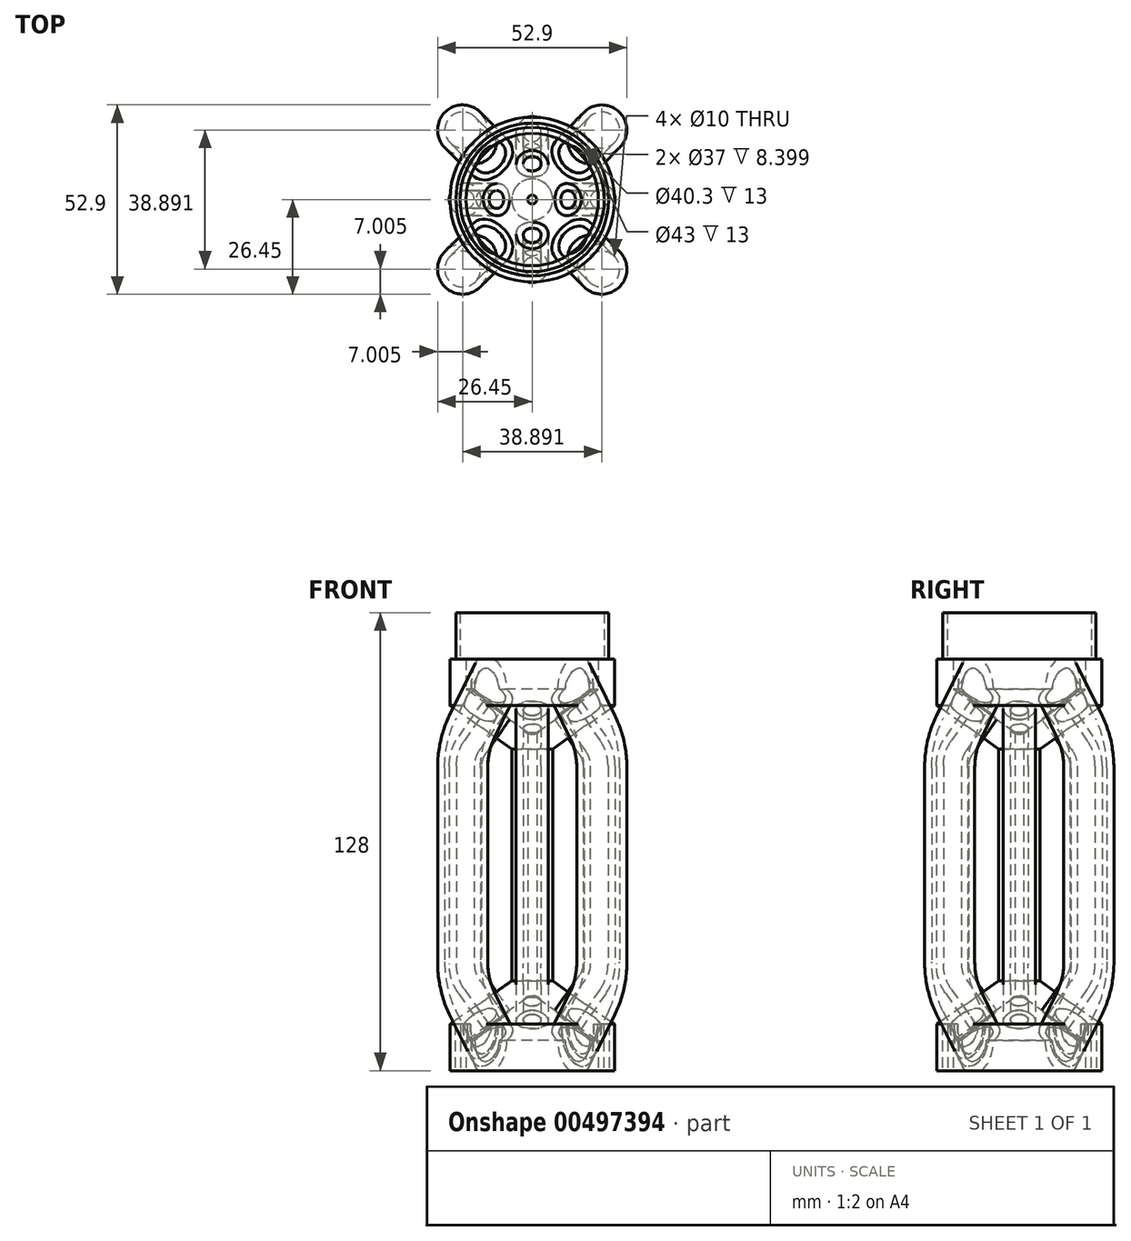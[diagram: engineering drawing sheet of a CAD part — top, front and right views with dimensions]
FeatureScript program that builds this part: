
annotation { "Feature Type Name" : "Feature", "Feature Type Description" : "" }
export const myFeature = defineFeature(function(context is Context, id is Id, definition is map)
    precondition{}
    {
        {
            var Q0;
            Q0=qCreatedBy(makeId("Front.planeOp"),FACE);
            var sketch = newSketch(context, id + "F0", { "sketchPlane" : qUnion([Q0])});
            skLineSegment(sketch, "E0", {"start": v(0, 0) * mm, "end": v(23, 0) * mm});
            skLineSegment(sketch, "E1.bottom", {"start": v(23, 0) * mm, "end": v(21.5, 0) * mm});
            skLineSegment(sketch, "E1.top", {"start": v(23, -13) * mm, "end": v(21.5, -13) * mm});
            skLineSegment(sketch, "E1.left", {"start": v(23, 0) * mm, "end": v(23, -13) * mm});
            skLineSegment(sketch, "E1.right", {"start": v(21.5, 0) * mm, "end": v(21.5, -13) * mm});
            skLineSegment(sketch, "E2.bottom", {"start": v(21.5, 0) * mm, "end": v(20, 0) * mm});
            skLineSegment(sketch, "E2.top", {"start": v(21.5, -13) * mm, "end": v(20, -13) * mm});
            skLineSegment(sketch, "E2.right", {"start": v(20, 0) * mm, "end": v(20, -13) * mm});
            skLineSegment(sketch, "E3.bottom", {"start": v(20, -13) * mm, "end": v(18.5, -13) * mm});
            skLineSegment(sketch, "E3.top", {"start": v(20, 0) * mm, "end": v(18.5, 0) * mm});
            skLineSegment(sketch, "E3.left", {"start": v(20, -13) * mm, "end": v(20, 0) * mm});
            skLineSegment(sketch, "E3.right", {"start": v(18.5, -13) * mm, "end": v(18.5, 0) * mm});
            skLineSegment(sketch, "E4.bottom", {"start": v(23, 0) * mm, "end": v(0, 0) * mm});
            skLineSegment(sketch, "E4.top", {"start": v(23, 102) * mm, "end": v(0, 102) * mm});
            skLineSegment(sketch, "E4.left", {"start": v(23, 0) * mm, "end": v(23, 102) * mm});
            skLineSegment(sketch, "E4.right", {"start": v(0, 0) * mm, "end": v(0, 102) * mm});
            skLineSegment(sketch, "E5.bottom", {"start": v(21.35, 102) * mm, "end": v(20.15, 102) * mm});
            skLineSegment(sketch, "E5.top", {"start": v(21.35, 115) * mm, "end": v(20.15, 115) * mm});
            skLineSegment(sketch, "E5.left", {"start": v(21.35, 102) * mm, "end": v(21.35, 115) * mm});
            skLineSegment(sketch, "E5.right", {"start": v(20.15, 102) * mm, "end": v(20.15, 115) * mm});
            skLineSegment(sketch, "E6", {"start": v(0, 44.5) * mm, "end": v(23, 44.5) * mm});
            skLineSegment(sketch, "E7.0", {"start": v(18.5, 0) * mm, "end": v(18.5, 102) * mm});
            skPoint(sketch, "E8.endSnap0", {"position": v(11.5, 44.5) * mm});
            skLineSegment(sketch, "E9", {"start": v(11.5, 44.5) * mm, "end": v(0, 44.5) * mm});
            skPoint(sketch, "E10", {"position": v(5.75, 44.5) * mm});
            skLineSegment(sketch, "E11", {"start": v(23, 0) * mm, "end": v(5.75, 7.47) * mm});
            skLineSegment(sketch, "E12", {"start": v(5.75, 7.47) * mm, "end": v(5.75, 44.5) * mm});
            skLineSegment(sketch, "E13.0", {"start": v(1.25, 4.51) * mm, "end": v(1.25, 44.5) * mm});
            skLineSegment(sketch, "E13.1", {"start": v(20.46, -3.8) * mm, "end": v(1.25, 4.51) * mm});
            skLineSegment(sketch, "E14.MirrorCS", {"start": v(5.75, 81.53) * mm, "end": v(5.75, 44.5) * mm});
            skLineSegment(sketch, "E15.MirrorCS", {"start": v(1.25, 84.49) * mm, "end": v(1.25, 44.5) * mm});
            skLineSegment(sketch, "E16.MirrorCS", {"start": v(20.46, 92.8) * mm, "end": v(1.25, 84.49) * mm});
            skLineSegment(sketch, "E17.MirrorCS", {"start": v(23, 89) * mm, "end": v(5.75, 81.53) * mm});
            skLineSegment(sketch, "E18", {"start": v(23, 0) * mm, "end": v(5.75, 12.08) * mm});
            skLineSegment(sketch, "E19.0", {"start": v(19.36, -5.2) * mm, "end": v(-0.63, 8.8) * mm});
            skLineSegment(sketch, "E20", {"start": v(1.25, 7.48) * mm, "end": v(-0.55, 8.74) * mm});
            skLineSegment(sketch, "E21.MirrorCS", {"start": v(19.36, 94.2) * mm, "end": v(-0.63, 80.2) * mm});
            skLineSegment(sketch, "E22.MirrorCS", {"start": v(23, 89) * mm, "end": v(5.75, 76.92) * mm});
            skLineSegment(sketch, "E23.MirrorCS", {"start": v(1.25, 81.52) * mm, "end": v(-0.55, 80.26) * mm});
            skSolve(sketch);
        }
        {
            var Q0;
            Q0=makeQuery(id+"F0.imprint","IMPRINT",FACE,{"disambiguationData":[TD([[makeQuery(id+"F0.imprint","IMPRINT",EDGE,{"derivedFrom":sQuery(id+"F0.wireOp",EDGE,"E1.top")}),-1.0]])]});
            var Q1;
            {var subQ1=sQuery(id+"F0.wireOp",EDGE,"E3.bottom");Q1=makeQuery(id+"F0.imprint","IMPRINT",FACE,{"disambiguationData":[TD([[makeQuery(id+"F0.imprint","IMPRINT",EDGE,{"derivedFrom":subQ1}),-1.0]])]});}
            var Q2;
            {var subQ3=sQuery(id+"F0.wireOp",EDGE,"E0");var subQ6=makeQuery(id+"F0.imprint","INTERSECT",VERTEX,{"derivedFrom":[subQ3,sQuery(id+"F0.wireOp",EDGE,"E1.right")]});Q2=makeQuery(id+"F0.imprint","IMPRINT",FACE,{"disambiguationData":[TD([[makeQuery(id+"F0.imprint","IMPRINT",EDGE,{"disambiguationData":[TD([[subQ6,1.0]])],"derivedFrom":subQ3}),1.0]])]});}
            var Q3;
            {var subQ0=sQuery(id+"F0.wireOp",EDGE,"E4.top");var subQ7=sQuery(id+"F0.wireOp",EDGE,"E4.left");var subQ8=makeQuery(id+"F0.imprint","INTERSECT",VERTEX,{"derivedFrom":[subQ0,subQ7]});Q3=makeQuery(id+"F0.imprint","IMPRINT",FACE,{"disambiguationData":[TD([[makeQuery(id+"F0.imprint","IMPRINT",EDGE,{"disambiguationData":[TD([[subQ8,-1.0]])],"derivedFrom":subQ0}),1.0]])]});}
            var Q4;
            Q4=makeQuery(id+"F0.imprint","IMPRINT",FACE,{"disambiguationData":[TD([[makeQuery(id+"F0.imprint","IMPRINT",EDGE,{"derivedFrom":sQuery(id+"F0.wireOp",EDGE,"E5.top")}),1.0]])]});
            var Q5;
            {var subQ0=sQuery(id+"F0.wireOp",EDGE,"E2.right");var subQ5=sQuery(id+"F0.wireOp",EDGE,"E13.1");var subQ7=makeQuery(id+"F0.imprint","INTERSECT",VERTEX,{"derivedFrom":[subQ0,subQ5]});Q5=makeQuery(id+"F0.imprint","IMPRINT",FACE,{"disambiguationData":[TD([[makeQuery(id+"F0.imprint","IMPRINT",EDGE,{"disambiguationData":[TD([[subQ7,1.0]])],"derivedFrom":subQ0}),-1.0]])]});}
            var Q6;
            {var subQ3=sQuery(id+"F0.wireOp",EDGE,"E3.right");var subQ5=sQuery(id+"F0.wireOp",EDGE,"E13.1");var subQ7=makeQuery(id+"F0.imprint","INTERSECT",VERTEX,{"derivedFrom":[subQ3,subQ5]});Q6=makeQuery(id+"F0.imprint","IMPRINT",FACE,{"disambiguationData":[TD([[makeQuery(id+"F0.imprint","IMPRINT",EDGE,{"disambiguationData":[TD([[subQ7,-1.0]])],"derivedFrom":subQ5}),-1.0]])]});}
            var Q7;
            {var subQ0=sQuery(id+"F0.wireOp",EDGE,"E11");var subQ1=sQuery(id+"F0.wireOp",EDGE,"E7.0");var subQ2=makeQuery(id+"F0.imprint","INTERSECT",VERTEX,{"derivedFrom":[subQ1,subQ0]});Q7=makeQuery(id+"F0.imprint","IMPRINT",FACE,{"disambiguationData":[TD([[makeQuery(id+"F0.imprint","IMPRINT",EDGE,{"disambiguationData":[TD([[subQ2,-1.0]])],"derivedFrom":subQ0}),1.0]])]});}
            var Q8;
            {var subQ2=sQuery(id+"F0.wireOp",EDGE,"E17.MirrorCS");var subQ8=sQuery(id+"F0.wireOp",EDGE,"E7.0");var subQ9=makeQuery(id+"F0.imprint","INTERSECT",VERTEX,{"derivedFrom":[subQ8,subQ2]});Q8=makeQuery(id+"F0.imprint","IMPRINT",FACE,{"disambiguationData":[TD([[makeQuery(id+"F0.imprint","IMPRINT",EDGE,{"disambiguationData":[TD([[subQ9,-1.0]])],"derivedFrom":subQ8}),1.0]])]});}
            var Q9;
            {var subQ0=sQuery(id+"F0.wireOp",EDGE,"E18");var subQ1=sQuery(id+"F0.wireOp",EDGE,"E7.0");var subQ2=makeQuery(id+"F0.imprint","INTERSECT",VERTEX,{"derivedFrom":[subQ1,subQ0]});Q9=makeQuery(id+"F0.imprint","IMPRINT",FACE,{"disambiguationData":[TD([[makeQuery(id+"F0.imprint","IMPRINT",EDGE,{"disambiguationData":[TD([[subQ2,1.0]])],"derivedFrom":subQ1}),1.0]])]});}
            var Q10;
            {var subQ0=sQuery(id+"F0.wireOp",EDGE,"E18");var subQ1=sQuery(id+"F0.wireOp",EDGE,"E7.0");var subQ2=makeQuery(id+"F0.imprint","INTERSECT",VERTEX,{"derivedFrom":[subQ1,subQ0]});Q10=makeQuery(id+"F0.imprint","IMPRINT",FACE,{"disambiguationData":[TD([[makeQuery(id+"F0.imprint","IMPRINT",EDGE,{"disambiguationData":[TD([[subQ2,1.0]])],"derivedFrom":subQ1}),-1.0]])]});}
            var Q11;
            {var subQ0=sQuery(id+"F0.wireOp",EDGE,"E11");var subQ1=sQuery(id+"F0.wireOp",EDGE,"E7.0");var subQ2=makeQuery(id+"F0.imprint","INTERSECT",VERTEX,{"derivedFrom":[subQ1,subQ0]});Q11=makeQuery(id+"F0.imprint","IMPRINT",FACE,{"disambiguationData":[TD([[makeQuery(id+"F0.imprint","IMPRINT",EDGE,{"disambiguationData":[TD([[subQ2,-1.0]])],"derivedFrom":subQ0}),1.0]])]});}
            var Q12;
            {var subQ0=sQuery(id+"F0.wireOp",EDGE,"E13.1");var subQ1=sQuery(id+"F0.wireOp",EDGE,"E3.right");var subQ2=makeQuery(id+"F0.imprint","INTERSECT",VERTEX,{"derivedFrom":[subQ1,subQ0]});Q12=makeQuery(id+"F0.imprint","IMPRINT",FACE,{"disambiguationData":[TD([[makeQuery(id+"F0.imprint","IMPRINT",EDGE,{"disambiguationData":[TD([[subQ2,1.0]])],"derivedFrom":subQ1}),1.0]])]});}
            var Q13;
            {var subQ0=sQuery(id+"F0.wireOp",EDGE,"E17.MirrorCS");var subQ1=sQuery(id+"F0.wireOp",EDGE,"E7.0");var subQ2=makeQuery(id+"F0.imprint","INTERSECT",VERTEX,{"derivedFrom":[subQ1,subQ0]});Q13=makeQuery(id+"F0.imprint","IMPRINT",FACE,{"disambiguationData":[TD([[makeQuery(id+"F0.imprint","IMPRINT",EDGE,{"disambiguationData":[TD([[subQ2,1.0]])],"derivedFrom":subQ1}),1.0]])]});}
            var Q14;
            {var subQ2=sQuery(id+"F0.wireOp",EDGE,"E17.MirrorCS");var subQ8=sQuery(id+"F0.wireOp",EDGE,"E7.0");var subQ9=makeQuery(id+"F0.imprint","INTERSECT",VERTEX,{"derivedFrom":[subQ8,subQ2]});Q14=makeQuery(id+"F0.imprint","IMPRINT",FACE,{"disambiguationData":[TD([[makeQuery(id+"F0.imprint","IMPRINT",EDGE,{"disambiguationData":[TD([[subQ9,-1.0]])],"derivedFrom":subQ8}),1.0]])]});}
            var Q15;
            {var subQ0=sQuery(id+"F0.wireOp",EDGE,"E17.MirrorCS");var subQ1=sQuery(id+"F0.wireOp",EDGE,"E7.0");var subQ2=makeQuery(id+"F0.imprint","INTERSECT",VERTEX,{"derivedFrom":[subQ1,subQ0]});Q15=makeQuery(id+"F0.imprint","IMPRINT",FACE,{"disambiguationData":[TD([[makeQuery(id+"F0.imprint","IMPRINT",EDGE,{"disambiguationData":[TD([[subQ2,1.0]])],"derivedFrom":subQ1}),-1.0]])]});}
            var Q16;
            {var subQ0=sQuery(id+"F0.wireOp",EDGE,"E16.MirrorCS");var subQ1=sQuery(id+"F0.wireOp",EDGE,"E7.0");var subQ2=makeQuery(id+"F0.imprint","INTERSECT",VERTEX,{"derivedFrom":[subQ1,subQ0]});Q16=makeQuery(id+"F0.imprint","IMPRINT",FACE,{"disambiguationData":[TD([[makeQuery(id+"F0.imprint","IMPRINT",EDGE,{"disambiguationData":[TD([[subQ2,-1.0]])],"derivedFrom":subQ1}),1.0]])]});}
            var Q17;
            Q17=sQuery(id+"F0.wireOp",EDGE,"E4.right");
            revolve(context, id + "F1", {"entities" : qUnion([Q0, Q1, Q2, Q3, Q4, Q5, Q6, Q7, Q8, Q9, Q10, Q11, Q12, Q13, Q14, Q15, Q16]), "axis" : qUnion([Q17]), "revolveType" : RevolveType.FULL, "surfaceOperationType" : NewSurfaceOperationType.NEW});
        }
        {
            var Q0;
            Q0=makeQuery(id+"F1.opRevolve","SWEPT_FACE",FACE,{"disambiguationData":[OSD([sQuery(id+"F0.wireOp",EDGE,"E3.bottom")])]});
            var sketch = newSketch(context, id + "F2", { "sketchPlane" : qUnion([Q0])});
            skCircle(sketch, "E24.0", {"center": v(0, 0) * mm, "radius": 18.5 * mm});
            skLineSegment(sketch, "E25", {"start": v(18.5, 0) * mm, "end": v(-18.5, 0) * mm});
            skLineSegment(sketch, "E26", {"start": v(0, 18.5) * mm, "end": v(0, -18.5) * mm});
            skLineSegment(sketch, "E27", {"start": v(0, 0) * mm, "end": v(18.5, 0) * mm});
            skLineSegment(sketch, "E28", {"start": v(0, -18.5) * mm, "end": v(0, 0) * mm});
            skLineSegment(sketch, "E29", {"start": v(-18.5, 0) * mm, "end": v(0, 0) * mm});
            skLineSegment(sketch, "E30", {"start": v(0, 0) * mm, "end": v(0, 18.5) * mm});
            skPoint(sketch, "E31", {"position": v(9.25, 0) * mm});
            skPoint(sketch, "E32", {"position": v(0, -9.25) * mm});
            skPoint(sketch, "E33", {"position": v(-9.25, 0) * mm});
            skPoint(sketch, "E34", {"position": v(0, 9.25) * mm});
            skLineSegment(sketch, "E35", {"start": v(-9.25, 0) * mm, "end": v(-18.5, 0) * mm});
            skLineSegment(sketch, "E36", {"start": v(0, 9.25) * mm, "end": v(0, 18.5) * mm});
            skLineSegment(sketch, "E37", {"start": v(0, -9.25) * mm, "end": v(0, -18.5) * mm});
            skLineSegment(sketch, "E38", {"start": v(9.25, 0) * mm, "end": v(18.5, 0) * mm});
            skPoint(sketch, "E39", {"position": v(13.87, 0) * mm});
            skPoint(sketch, "E40", {"position": v(0, -13.87) * mm});
            skPoint(sketch, "E41", {"position": v(-13.87, 0) * mm});
            skPoint(sketch, "E42", {"position": v(0, 13.87) * mm});
            skCircle(sketch, "E43", {"center": v(13.87, 0) * mm, "radius": 13.87 * mm});
            skCircle(sketch, "E44", {"center": v(0, -13.87) * mm, "radius": 13.87 * mm});
            skCircle(sketch, "E45", {"center": v(-13.87, 0) * mm, "radius": 13.87 * mm});
            skCircle(sketch, "E46", {"center": v(0, 13.87) * mm, "radius": 13.87 * mm});
            skLineSegment(sketch, "E47", {"start": v(0, 0) * mm, "end": v(13.87, 13.87) * mm});
            skLineSegment(sketch, "E48", {"start": v(-13.87, -13.87) * mm, "end": v(0, 0) * mm});
            skLineSegment(sketch, "E49", {"start": v(13.87, -13.87) * mm, "end": v(0, 0) * mm});
            skLineSegment(sketch, "E50", {"start": v(-13.87, 13.87) * mm, "end": v(0, 0) * mm});
            skPoint(sketch, "E51", {"position": v(-4.06, -9.81) * mm});
            skPoint(sketch, "E52", {"position": v(4.06, 9.81) * mm});
            skPoint(sketch, "E53", {"position": v(9.81, -4.06) * mm});
            skPoint(sketch, "E54", {"position": v(-9.81, 4.06) * mm});
            skSolve(sketch);
        }
        {
            var Q0;
            Q0=qCreatedBy(makeId("Front.planeOp"),FACE);
            var sketch = newSketch(context, id + "F3", { "sketchPlane" : qUnion([Q0])});
            skLineSegment(sketch, "E55", {"start": v(-23, -13) * mm, "end": v(-23, 0) * mm});
            skLineSegment(sketch, "E56", {"start": v(23, 0) * mm, "end": v(23, -13) * mm});
            skLineSegment(sketch, "E57.0", {"start": v(5.75, 12.08) * mm, "end": v(-5.75, 12.08) * mm});
            skLineSegment(sketch, "E58", {"start": v(-23, 0) * mm, "end": v(-5.75, 12.08) * mm});
            skLineSegment(sketch, "E59", {"start": v(5.75, 12.08) * mm, "end": v(23, 0) * mm});
            skLineSegment(sketch, "E60", {"start": v(-5.75, 12.08) * mm, "end": v(-5.75, 76.92) * mm});
            skLineSegment(sketch, "E61", {"start": v(5.75, 76.92) * mm, "end": v(5.75, 12.08) * mm});
            skLineSegment(sketch, "E62", {"start": v(23, 89) * mm, "end": v(5.75, 76.92) * mm});
            skLineSegment(sketch, "E63", {"start": v(-5.75, 76.92) * mm, "end": v(-23, 89) * mm});
            skLineSegment(sketch, "E64", {"start": v(-23, 89) * mm, "end": v(-23, 102) * mm});
            skLineSegment(sketch, "E65", {"start": v(23, 102) * mm, "end": v(23, 89) * mm});
            skLineSegment(sketch, "E66", {"start": v(-21.35, 102) * mm, "end": v(-21.35, 115) * mm});
            skLineSegment(sketch, "E67", {"start": v(21.35, 115) * mm, "end": v(21.35, 102) * mm});
            skLineSegment(sketch, "E68.0", {"start": v(23, 89) * mm, "end": v(-23, 89) * mm});
            skLineSegment(sketch, "E69.0", {"start": v(5.75, 76.92) * mm, "end": v(-5.75, 76.92) * mm});
            skLineSegment(sketch, "E70.0", {"start": v(23, 0) * mm, "end": v(-23, 0) * mm});
            skLineSegment(sketch, "E71.0", {"start": v(23, -13) * mm, "end": v(-23, -13) * mm});
            skLineSegment(sketch, "E72.0", {"start": v(23, 102) * mm, "end": v(-23, 102) * mm});
            skLineSegment(sketch, "E73.0", {"start": v(21.35, 115) * mm, "end": v(-21.35, 115) * mm});
            skLineSegment(sketch, "E74.0", {"start": v(20.15, 102) * mm, "end": v(-20.15, 102) * mm});
            skLineSegment(sketch, "E75", {"start": v(-20.15, 102) * mm, "end": v(-20.15, 115) * mm});
            skLineSegment(sketch, "E76", {"start": v(20.15, 115) * mm, "end": v(20.15, 102) * mm});
            skLineSegment(sketch, "E77", {"start": v(-18.5, 93.6) * mm, "end": v(-18.5, 102) * mm});
            skLineSegment(sketch, "E78", {"start": v(18.5, 102) * mm, "end": v(18.5, 93.6) * mm});
            skLineSegment(sketch, "E79.0.0", {"start": v(-20.15, 102) * mm, "end": v(20.15, 102) * mm});
            skLineSegment(sketch, "E80", {"start": v(18.5, 93.6) * mm, "end": v(1.25, 81.52) * mm});
            skLineSegment(sketch, "E81", {"start": v(-1.25, 81.52) * mm, "end": v(-18.5, 93.6) * mm});
            skLineSegment(sketch, "E82.0", {"start": v(1.25, 81.52) * mm, "end": v(-1.25, 81.52) * mm});
            skLineSegment(sketch, "E83", {"start": v(-18.5, -4.6) * mm, "end": v(-1.25, 7.48) * mm});
            skLineSegment(sketch, "E84", {"start": v(1.25, 7.48) * mm, "end": v(18.5, -4.6) * mm});
            skLineSegment(sketch, "E85", {"start": v(-18.5, -13) * mm, "end": v(-18.5, -4.6) * mm});
            skLineSegment(sketch, "E86", {"start": v(18.5, -4.6) * mm, "end": v(18.5, -13) * mm});
            skLineSegment(sketch, "E87.0.0", {"start": v(20, -13) * mm, "end": v(-20, -13) * mm});
            skLineSegment(sketch, "E88.0", {"start": v(1.25, 7.48) * mm, "end": v(-1.25, 7.48) * mm});
            skPoint(sketch, "E89.endSnap0", {"position": v(0, 102) * mm});
            skPoint(sketch, "E90", {"position": v(14.37, 6.04) * mm});
            skPoint(sketch, "E91", {"position": v(14.38, 82.96) * mm});
            skLineSegment(sketch, "E92", {"start": v(14.38, 82.96) * mm, "end": v(23, 89) * mm});
            skLineSegment(sketch, "E93", {"start": v(0, 102) * mm, "end": v(16.88, 77.9) * mm});
            skLineSegment(sketch, "E94", {"start": v(5.75, 44.5) * mm, "end": v(18.69, 44.5) * mm});
            skPoint(sketch, "E95.newPointA", {"position": v(18.69, 85.98) * mm});
            skPoint(sketch, "E95.newPointB", {"position": v(18.69, 75.31) * mm});
            skArc(sketch, "E95.filletArc", {"start": v(18.69, 72.16) * mm, "mid": v(18.22, 75.17) * mm, "end": v(16.88, 77.9) * mm});
            skLineSegment(sketch, "E96", {"start": v(18.69, 72.16) * mm, "end": v(18.69, 44.5) * mm});
            skLineSegment(sketch, "E97.MirrorCS", {"start": v(18.69, 16.84) * mm, "end": v(18.69, 44.5) * mm});
            skArc(sketch, "E98.MirrorCS", {"start": v(18.69, 16.84) * mm, "mid": v(18.22, 13.83) * mm, "end": v(16.88, 11.1) * mm});
            skLineSegment(sketch, "E99.MirrorCS", {"start": v(0, -13) * mm, "end": v(16.88, 11.1) * mm});
            skSolve(sketch);
        }
        {
            var Q0;
            Q0=sQuery(id+"F3.wireOp",EDGE,"E93");
            var Q1;
            Q1=sQuery(id+"F3.wireOp",VERTEX,"E89.endSnap0");
            cPlane(context, id + "F4", {"entities" : qUnion([Q0, Q1]), "cplaneType" : CPlaneType.CURVE_POINT, "offset" : 25 * mm, "width" : 150 * mm, "height" : 150 * mm});
        }
        {
            var Q0;
            Q0=qCreatedBy(id+"F4.planeOp",FACE);
            var sketch = newSketch(context, id + "F5", { "sketchPlane" : qUnion([Q0])});
            skPoint(sketch, "E100.0", {"position": v(58.5, 0) * mm});
            skCircle(sketch, "E101", {"center": v(58.5, 0) * mm, "radius": 2.5 * mm});
            skCircle(sketch, "E102", {"center": v(58.5, 0) * mm, "radius": 4.5 * mm});
            skSolve(sketch);
        }
        {
            var Q0;
            Q0=makeQuery(id+"F5.imprint","IMPRINT",FACE,{"disambiguationData":[TD([[makeQuery(id+"F5.imprint","IMPRINT",EDGE,{"derivedFrom":sQuery(id+"F5.wireOp",EDGE,"E101")}),-1.0]])]});
            var Q1;
            Q1=sQuery(id+"F3.wireOp",EDGE,"E93");
            var Q2;
            Q2=sQuery(id+"F3.wireOp",EDGE,"E95.filletArc");
            var Q3;
            Q3=sQuery(id+"F3.wireOp",EDGE,"E96");
            var Q4;
            Q4=sQuery(id+"F3.wireOp",EDGE,"E97.MirrorCS");
            var Q5;
            Q5=sQuery(id+"F3.wireOp",EDGE,"E98.MirrorCS");
            var Q6;
            Q6=sQuery(id+"F3.wireOp",EDGE,"E99.MirrorCS");
            sweep(context, id + "F6", {"profiles" : qUnion([Q0]), "path" : qUnion([Q1, Q2, Q3, Q4, Q5, Q6])});
        }
        {
            var Q0;
            Q0=makeQuery(id+"F6.opSweep","SWEPT_BODY",BODY,{"disambiguationData":[OSD([sQuery(id+"F3.wireOp",EDGE,"E99.MirrorCS"),sQuery(id+"F5.wireOp",EDGE,"E101"),sQuery(id+"F5.wireOp",EDGE,"E102")])]});
            var Q1;
            Q1=sQuery(id+"F0.wireOp",EDGE,"E4.right");
            circularPattern(context, id + "F7", {"entities" : qUnion([Q0]), "axis" : qUnion([Q1]), "angle" : 360 * degree, "instanceCount" : 4, "equalSpace" : true});
        }
        {
            var Q0;
            Q0=sQuery(id+"F0.wireOp",EDGE,"E4.right");
            cPlane(context, id + "F8", {"entities" : qUnion([Q0]), "cplaneType" : CPlaneType.LINE_ANGLE, "offset" : 25 * mm, "angle" : 45 * degree, "width" : 150 * mm, "height" : 150 * mm});
        }
        {
            var Q0;
            Q0=qCreatedBy(id+"F8.planeOp",FACE);
            var sketch = newSketch(context, id + "F9", { "sketchPlane" : qUnion([Q0])});
            skLineSegment(sketch, "E103", {"start": v(-23, -13) * mm, "end": v(-23, 0) * mm});
            skLineSegment(sketch, "E104", {"start": v(23, 0) * mm, "end": v(23, -13) * mm});
            skLineSegment(sketch, "E105", {"start": v(-23, 0) * mm, "end": v(-5.75, 12.08) * mm});
            skLineSegment(sketch, "E106", {"start": v(5.75, 12.08) * mm, "end": v(23, 0) * mm});
            skLineSegment(sketch, "E107.0", {"start": v(0, 0) * mm, "end": v(0, 102) * mm});
            skLineSegment(sketch, "E108", {"start": v(-5.75, 12.08) * mm, "end": v(-5.75, 76.92) * mm});
            skLineSegment(sketch, "E109", {"start": v(5.75, 76.92) * mm, "end": v(5.75, 12.08) * mm});
            skLineSegment(sketch, "E110", {"start": v(23, 89) * mm, "end": v(5.75, 76.92) * mm});
            skLineSegment(sketch, "E111", {"start": v(-5.75, 76.92) * mm, "end": v(-23, 89) * mm});
            skLineSegment(sketch, "E112", {"start": v(-23, 89) * mm, "end": v(-23, 102) * mm});
            skLineSegment(sketch, "E113", {"start": v(23, 102) * mm, "end": v(23, 89) * mm});
            skLineSegment(sketch, "E114", {"start": v(-21.35, 102) * mm, "end": v(-21.35, 115) * mm});
            skLineSegment(sketch, "E115", {"start": v(21.35, 115) * mm, "end": v(21.35, 102) * mm});
            skLineSegment(sketch, "E116.0", {"start": v(18.5, 102) * mm, "end": v(-18.5, 102) * mm});
            skLineSegment(sketch, "E117", {"start": v(18.5, 93.6) * mm, "end": v(1.25, 81.52) * mm});
            skLineSegment(sketch, "E118", {"start": v(-1.25, 81.52) * mm, "end": v(-18.5, 93.6) * mm});
            skLineSegment(sketch, "E119", {"start": v(-20.15, 102) * mm, "end": v(-20.15, 115) * mm});
            skLineSegment(sketch, "E120", {"start": v(20.15, 115) * mm, "end": v(20.15, 102) * mm});
            skLineSegment(sketch, "E121.0", {"start": v(18.5, 93.6) * mm, "end": v(-18.5, 93.6) * mm});
            skLineSegment(sketch, "E122", {"start": v(-18.5, 93.6) * mm, "end": v(-18.5, 102) * mm});
            skLineSegment(sketch, "E123", {"start": v(18.5, 102) * mm, "end": v(18.5, 93.6) * mm});
            skLineSegment(sketch, "E124.0.0", {"start": v(-20.15, 102) * mm, "end": v(20.15, 102) * mm});
            skLineSegment(sketch, "E125.0.0", {"start": v(-21.35, 115) * mm, "end": v(21.35, 115) * mm});
            skLineSegment(sketch, "E126.0.0", {"start": v(-23, 102) * mm, "end": v(23, 102) * mm});
            skLineSegment(sketch, "E127", {"start": v(-18.5, -4.6) * mm, "end": v(-1.25, 7.48) * mm});
            skLineSegment(sketch, "E128", {"start": v(1.25, 7.48) * mm, "end": v(18.5, -4.6) * mm});
            skLineSegment(sketch, "E129", {"start": v(-18.5, -13) * mm, "end": v(-18.5, -4.6) * mm});
            skLineSegment(sketch, "E130", {"start": v(18.5, -4.6) * mm, "end": v(18.5, -13) * mm});
            skLineSegment(sketch, "E131.0", {"start": v(23, -13) * mm, "end": v(-23, -13) * mm});
            skLineSegment(sketch, "E132", {"start": v(-17.71, 16.84) * mm, "end": v(-17.71, 72.16) * mm});
            skLineSegment(sketch, "E133", {"start": v(-8.71, 72.16) * mm, "end": v(-8.71, 16.84) * mm});
            skLineSegment(sketch, "E134", {"start": v(8.71, 16.84) * mm, "end": v(8.71, 72.16) * mm});
            skLineSegment(sketch, "E135", {"start": v(17.71, 72.16) * mm, "end": v(17.71, 16.84) * mm});
            skFitSpline(sketch, "E136", {"points": [v(-15.97, 9.1) * mm, v(-16.53, 10.25) * mm, v(-17.41, 12.74) * mm, v(-17.71, 15.48) * mm, v(-17.71, 16.84) * mm]});
            skFitSpline(sketch, "E137", {"points": [v(-8.71, 16.84) * mm, v(-8.71, 16.14) * mm, v(-8.55, 14.72) * mm, v(-8.13, 13.57) * mm, v(-7.9, 13.1) * mm]});
            skLineSegment(sketch, "E138", {"start": v(-4.03, -15) * mm, "end": v(-15.97, 9.1) * mm});
            skLineSegment(sketch, "E139", {"start": v(-7.9, 13.1) * mm, "end": v(4.03, -11) * mm});
            skLineSegment(sketch, "E140", {"start": v(-4.03, -11) * mm, "end": v(7.9, 13.1) * mm});
            skLineSegment(sketch, "E141", {"start": v(15.97, 9.1) * mm, "end": v(4.03, -15) * mm});
            skFitSpline(sketch, "E142", {"points": [v(7.9, 13.1) * mm, v(8.13, 13.57) * mm, v(8.55, 14.72) * mm, v(8.71, 16.14) * mm, v(8.71, 16.84) * mm]});
            skFitSpline(sketch, "E143", {"points": [v(17.71, 16.84) * mm, v(17.71, 15.48) * mm, v(17.41, 12.74) * mm, v(16.53, 10.25) * mm, v(15.97, 9.1) * mm]});
            skLineSegment(sketch, "E144", {"start": v(-15.97, 79.9) * mm, "end": v(-4.03, 104) * mm});
            skLineSegment(sketch, "E145", {"start": v(4.03, 100) * mm, "end": v(-7.9, 75.9) * mm});
            skLineSegment(sketch, "E146", {"start": v(7.9, 75.9) * mm, "end": v(-4.03, 100) * mm});
            skLineSegment(sketch, "E147", {"start": v(4.03, 104) * mm, "end": v(15.97, 79.9) * mm});
            skFitSpline(sketch, "E148", {"points": [v(8.71, 72.16) * mm, v(8.71, 72.86) * mm, v(8.55, 74.28) * mm, v(8.13, 75.43) * mm, v(7.9, 75.9) * mm]});
            skFitSpline(sketch, "E149", {"points": [v(15.97, 79.9) * mm, v(16.53, 78.75) * mm, v(17.41, 76.26) * mm, v(17.71, 73.52) * mm, v(17.71, 72.16) * mm]});
            skFitSpline(sketch, "E150", {"points": [v(-17.71, 72.16) * mm, v(-17.71, 73.52) * mm, v(-17.41, 76.26) * mm, v(-16.53, 78.75) * mm, v(-15.97, 79.9) * mm]});
            skFitSpline(sketch, "E151", {"points": [v(-7.9, 75.9) * mm, v(-8.13, 75.43) * mm, v(-8.55, 74.28) * mm, v(-8.71, 72.86) * mm, v(-8.71, 72.16) * mm]});
            skPoint(sketch, "E152", {"position": v(-10.62, 102) * mm});
            skLineSegment(sketch, "E153", {"start": v(1.25, 81.52) * mm, "end": v(-1.25, 81.52) * mm});
            skLineSegment(sketch, "E154", {"start": v(1.25, 7.48) * mm, "end": v(-1.25, 7.48) * mm});
            skLineSegment(sketch, "E155", {"start": v(0, 81.52) * mm, "end": v(0, 7.48) * mm});
            skLineSegment(sketch, "E156", {"start": v(-27.5, 44.5) * mm, "end": v(-27.5, 71.58) * mm});
            skLineSegment(sketch, "E157", {"start": v(-23.88, 83.05) * mm, "end": v(-10.62, 102) * mm});
            skLineSegment(sketch, "E158", {"start": v(-27.5, 44.5) * mm, "end": v(0, 44.5) * mm});
            skPoint(sketch, "E159.visualSharp", {"position": v(-27.5, 77.89) * mm});
            skArc(sketch, "E159.filletArc", {"start": v(-23.88, 83.05) * mm, "mid": v(-26.57, 77.6) * mm, "end": v(-27.5, 71.58) * mm});
            skArc(sketch, "E160.MirrorCS", {"start": v(-23.88, 5.95) * mm, "mid": v(-26.57, 11.4) * mm, "end": v(-27.5, 17.42) * mm});
            skPoint(sketch, "E161", {"position": v(-10.62, -13) * mm});
            skLineSegment(sketch, "E162", {"start": v(-23.88, 5.95) * mm, "end": v(-10.62, -13) * mm});
            skLineSegment(sketch, "E163", {"start": v(-27.5, 17.42) * mm, "end": v(-27.5, 44.5) * mm});
            skSolve(sketch);
        }
        {
            var Q0;
            Q0=sQuery(id+"F9.wireOp",EDGE,"E157");
            var Q1;
            Q1=sQuery(id+"F9.wireOp",VERTEX,"E152");
            cPlane(context, id + "F10", {"entities" : qUnion([Q0, Q1]), "cplaneType" : CPlaneType.CURVE_POINT, "offset" : 25 * mm, "width" : 150 * mm, "height" : 150 * mm});
        }
        {
            var Q0;
            Q0=qCreatedBy(id+"F10.planeOp",FACE);
            var sketch = newSketch(context, id + "F11", { "sketchPlane" : qUnion([Q0])});
            skPoint(sketch, "E164.0", {"position": v(42.59, -51.99) * mm});
            skCircle(sketch, "E165", {"center": v(42.59, -51.99) * mm, "radius": 5 * mm});
            skCircle(sketch, "E166", {"center": v(42.59, -51.99) * mm, "radius": 7 * mm});
            skSolve(sketch);
        }
        {
            var Q0;
            Q0=makeQuery(id+"F11.imprint","IMPRINT",FACE,{"disambiguationData":[TD([[makeQuery(id+"F11.imprint","IMPRINT",EDGE,{"derivedFrom":sQuery(id+"F11.wireOp",EDGE,"E165")}),-1.0]])]});
            var Q1;
            Q1=sQuery(id+"F9.wireOp",EDGE,"E157");
            var Q2;
            Q2=sQuery(id+"F9.wireOp",EDGE,"E159.filletArc");
            var Q3;
            Q3=sQuery(id+"F9.wireOp",EDGE,"E156");
            var Q4;
            Q4=sQuery(id+"F9.wireOp",EDGE,"E163");
            var Q5;
            Q5=sQuery(id+"F9.wireOp",EDGE,"E160.MirrorCS");
            var Q6;
            Q6=sQuery(id+"F9.wireOp",EDGE,"E162");
            sweep(context, id + "F12", {"profiles" : qUnion([Q0]), "path" : qUnion([Q1, Q2, Q3, Q4, Q5, Q6])});
        }
        {
            var Q0;
            Q0=makeQuery(id+"F12.opSweep","SWEPT_BODY",BODY,{"disambiguationData":[OSD([sQuery(id+"F9.wireOp",EDGE,"E162"),sQuery(id+"F11.wireOp",EDGE,"E165"),sQuery(id+"F11.wireOp",EDGE,"E166")])]});
            var Q1;
            Q1=sQuery(id+"F0.wireOp",EDGE,"E4.right");
            circularPattern(context, id + "F13", {"entities" : qUnion([Q0]), "axis" : qUnion([Q1]), "angle" : 360 * degree, "instanceCount" : 4, "equalSpace" : true});
        }
        {
            var Q0;
            Q0=qCreatedBy(id+"F8.planeOp",FACE);
            var sketch = newSketch(context, id + "F14", { "sketchPlane" : qUnion([Q0])});
            skLineSegment(sketch, "E167", {"start": v(18.5, 93.6) * mm, "end": v(1.25, 81.52) * mm});
            skLineSegment(sketch, "E168", {"start": v(-1.25, 81.52) * mm, "end": v(-18.5, 93.6) * mm});
            skLineSegment(sketch, "E169", {"start": v(-18.5, 93.6) * mm, "end": v(-18.5, 102) * mm});
            skLineSegment(sketch, "E170", {"start": v(18.5, 102) * mm, "end": v(18.5, 93.6) * mm});
            skLineSegment(sketch, "E171", {"start": v(-20.15, 102) * mm, "end": v(-20.15, 115) * mm});
            skLineSegment(sketch, "E172", {"start": v(20.15, 115) * mm, "end": v(20.15, 102) * mm});
            skLineSegment(sketch, "E173", {"start": v(-18.5, -4.6) * mm, "end": v(-1.25, 7.48) * mm});
            skLineSegment(sketch, "E174", {"start": v(1.25, 7.48) * mm, "end": v(18.5, -4.6) * mm});
            skLineSegment(sketch, "E175", {"start": v(-18.5, -13) * mm, "end": v(-18.5, -4.6) * mm});
            skLineSegment(sketch, "E176", {"start": v(18.5, -4.6) * mm, "end": v(18.5, -13) * mm});
            skLineSegment(sketch, "E177", {"start": v(20.15, 115) * mm, "end": v(-20.15, 115) * mm});
            skLineSegment(sketch, "E178", {"start": v(20.15, 102) * mm, "end": v(-20.15, 102) * mm});
            skLineSegment(sketch, "E179", {"start": v(1.25, 81.52) * mm, "end": v(-1.25, 81.52) * mm});
            skLineSegment(sketch, "E180", {"start": v(1.25, 7.48) * mm, "end": v(-1.25, 7.48) * mm});
            skLineSegment(sketch, "E181", {"start": v(18.5, -13) * mm, "end": v(-18.5, -13) * mm});
            skLineSegment(sketch, "E182.top", {"start": v(18.5, -37.64) * mm, "end": v(-18.5, -37.64) * mm});
            skLineSegment(sketch, "E182.left", {"start": v(18.5, -13) * mm, "end": v(18.5, -37.64) * mm});
            skLineSegment(sketch, "E182.right", {"start": v(-18.5, -13) * mm, "end": v(-18.5, -37.64) * mm});
            skLineSegment(sketch, "E183", {"start": v(0, 115) * mm, "end": v(0, -37.64) * mm});
            skLineSegment(sketch, "E184", {"start": v(-21.5, -13) * mm, "end": v(-21.5, 0) * mm});
            skLineSegment(sketch, "E185", {"start": v(21.5, 0) * mm, "end": v(21.5, -13) * mm});
            skLineSegment(sketch, "E186", {"start": v(-20, -13) * mm, "end": v(-20, 0) * mm});
            skLineSegment(sketch, "E187", {"start": v(20, 0) * mm, "end": v(20, -13) * mm});
            skLineSegment(sketch, "E188", {"start": v(21.5, 0) * mm, "end": v(20, 0) * mm});
            skLineSegment(sketch, "E189", {"start": v(21.5, -13) * mm, "end": v(20, -13) * mm});
            skLineSegment(sketch, "E190.bottom", {"start": v(21.5, -13) * mm, "end": v(-21.5, -13) * mm});
            skLineSegment(sketch, "E190.top", {"start": v(21.5, -37.64) * mm, "end": v(-21.5, -37.64) * mm});
            skLineSegment(sketch, "E190.left", {"start": v(21.5, -13) * mm, "end": v(21.5, -37.64) * mm});
            skLineSegment(sketch, "E190.right", {"start": v(-21.5, -13) * mm, "end": v(-21.5, -37.64) * mm});
            skSolve(sketch);
        }
        {
            var Q0;
            {var subQ5=sQuery(id+"F14.wireOp",EDGE,"E174");Q0=makeQuery(id+"F14.imprint","IMPRINT",FACE,{"disambiguationData":[TD([[makeQuery(id+"F14.imprint","IMPRINT",EDGE,{"derivedFrom":subQ5}),-1.0]])]});}
            var Q1;
            {var subQ0=sQuery(id+"F14.wireOp",EDGE,"E182.left");Q1=makeQuery(id+"F14.imprint","IMPRINT",FACE,{"disambiguationData":[TD([[makeQuery(id+"F14.imprint","IMPRINT",EDGE,{"derivedFrom":subQ0}),-1.0]])]});}
            var Q2;
            Q2=makeQuery(id+"F14.imprint","IMPRINT",FACE,{"disambiguationData":[TD([[makeQuery(id+"F14.imprint","IMPRINT",EDGE,{"derivedFrom":sQuery(id+"F14.wireOp",EDGE,"E185")}),-1.0]])]});
            var Q3;
            {var subQ5=sQuery(id+"F14.wireOp",EDGE,"E172");Q3=makeQuery(id+"F14.imprint","IMPRINT",FACE,{"disambiguationData":[TD([[makeQuery(id+"F14.imprint","IMPRINT",EDGE,{"derivedFrom":subQ5}),-1.0]])]});}
            var Q4;
            {var subQ1=sQuery(id+"F14.wireOp",EDGE,"E167");Q4=makeQuery(id+"F14.imprint","IMPRINT",FACE,{"disambiguationData":[TD([[makeQuery(id+"F14.imprint","IMPRINT",EDGE,{"derivedFrom":subQ1}),-1.0]])]});}
            var Q5;
            {var subQ1=sQuery(id+"F14.wireOp",EDGE,"E182.left");Q5=makeQuery(id+"F14.imprint","IMPRINT",FACE,{"disambiguationData":[TD([[makeQuery(id+"F14.imprint","IMPRINT",EDGE,{"derivedFrom":subQ1}),1.0]])]});}
            var Q6;
            Q6=sQuery(id+"F14.wireOp",EDGE,"E183");
            revolve(context, id + "F15", {"operationType" : NewBodyOperationType.REMOVE, "surfaceOperationType" : NewSurfaceOperationType.NEW, "entities" : qUnion([Q0, Q1, Q2, Q3, Q4, Q5]), "axis" : qUnion([Q6]), "revolveType" : RevolveType.FULL, "oppositeDirection" : true});
        }
        {
            var Q0;
            Q0=makeQuery(id+"F11.imprint","IMPRINT",FACE,{"disambiguationData":[TD([[makeQuery(id+"F11.imprint","IMPRINT",EDGE,{"derivedFrom":sQuery(id+"F11.wireOp",EDGE,"E165")}),1.0]])]});
            var Q1;
            Q1=sQuery(id+"F9.wireOp",EDGE,"E157");
            var Q2;
            Q2=sQuery(id+"F9.wireOp",EDGE,"E159.filletArc");
            var Q3;
            Q3=sQuery(id+"F9.wireOp",EDGE,"E156");
            var Q4;
            Q4=sQuery(id+"F9.wireOp",EDGE,"E160.MirrorCS");
            var Q5;
            Q5=sQuery(id+"F9.wireOp",EDGE,"E163");
            var Q6;
            Q6=sQuery(id+"F9.wireOp",EDGE,"E162");
            sweep(context, id + "F16", {"profiles" : qUnion([Q0]), "path" : qUnion([Q1, Q2, Q3, Q4, Q5, Q6])});
        }
        {
            var Q0;
            Q0=makeQuery(id+"F5.imprint","IMPRINT",FACE,{"disambiguationData":[TD([[makeQuery(id+"F5.imprint","IMPRINT",EDGE,{"derivedFrom":sQuery(id+"F5.wireOp",EDGE,"E101")}),1.0]])]});
            var Q1;
            Q1=sQuery(id+"F3.wireOp",EDGE,"E93");
            var Q2;
            Q2=sQuery(id+"F3.wireOp",EDGE,"E95.filletArc");
            var Q3;
            Q3=sQuery(id+"F3.wireOp",EDGE,"E96");
            var Q4;
            Q4=sQuery(id+"F3.wireOp",EDGE,"E97.MirrorCS");
            var Q5;
            Q5=sQuery(id+"F3.wireOp",EDGE,"E98.MirrorCS");
            var Q6;
            Q6=sQuery(id+"F3.wireOp",EDGE,"E99.MirrorCS");
            sweep(context, id + "F17", {"profiles" : qUnion([Q0]), "path" : qUnion([Q1, Q2, Q3, Q4, Q5, Q6])});
        }
        {
            var Q0;
            Q0=makeQuery(id+"F17.opSweep","SWEPT_BODY",BODY,{"disambiguationData":[OSD([sQuery(id+"F3.wireOp",EDGE,"E99.MirrorCS"),sQuery(id+"F5.wireOp",EDGE,"E101")])]});
            var Q1;
            Q1=makeQuery(id+"F16.opSweep","SWEPT_BODY",BODY,{"disambiguationData":[OSD([sQuery(id+"F9.wireOp",EDGE,"E162"),sQuery(id+"F11.wireOp",EDGE,"E165")])]});
            var Q2;
            Q2=sQuery(id+"F0.wireOp",EDGE,"E4.right");
            circularPattern(context, id + "F18", {"operationType" : NewBodyOperationType.REMOVE, "entities" : qUnion([Q0, Q1]), "axis" : qUnion([Q2]), "angle" : 360 * degree, "instanceCount" : 4, "equalSpace" : true});
        }
    });
